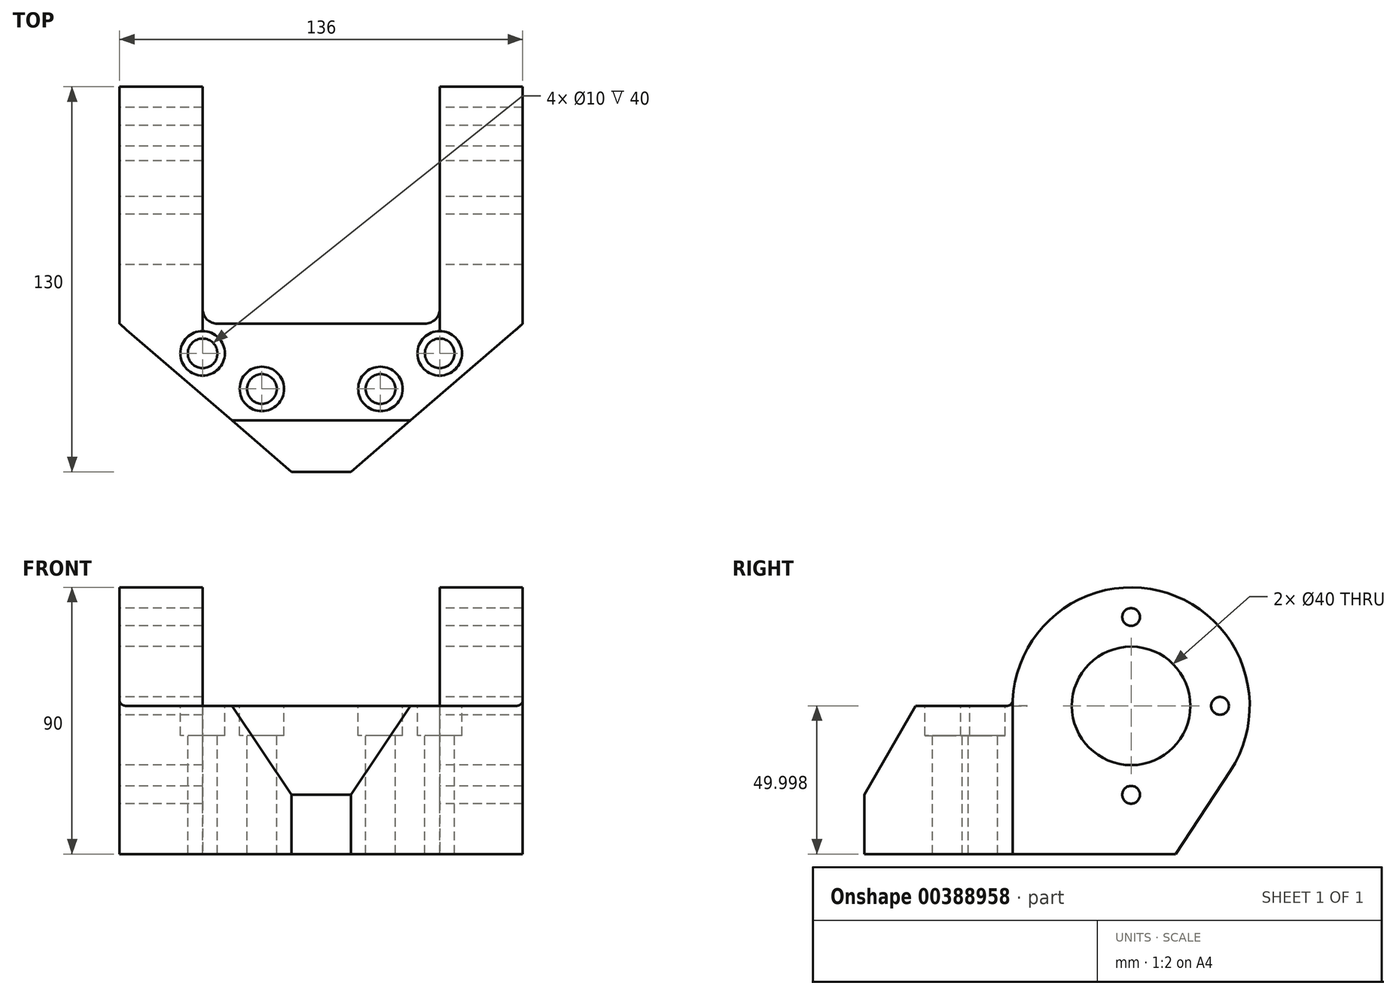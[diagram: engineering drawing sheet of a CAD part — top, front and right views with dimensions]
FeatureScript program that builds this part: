
annotation { "Feature Type Name" : "Feature", "Feature Type Description" : "" }
export const myFeature = defineFeature(function(context is Context, id is Id, definition is map)
    precondition{}
    {
        {
            var Q0;
            Q0=qCreatedBy(makeId("Right.planeOp"),FACE);
            var sketch = newSketch(context, id + "F0", { "sketchPlane" : qUnion([Q0])});
            skLineSegment(sketch, "E0.bottom", {"start": v(52.5, -26.77) * mm, "end": v(-52.5, -26.77) * mm});
            skPoint(sketch, "E0.middle", {"position": v(0, 0) * mm});
            skPoint(sketch, "E1", {"position": v(-52.5, -6.77) * mm});
            skLineSegment(sketch, "E2", {"start": v(-52.5, -6.77) * mm, "end": v(-35.18, 23.23) * mm});
            skPoint(sketch, "E3", {"position": v(37.5, 23.23) * mm});
            skLineSegment(sketch, "E4", {"start": v(-52.5, -26.77) * mm, "end": v(-52.5, -6.77) * mm});
            skCircle(sketch, "E5", {"center": v(37.5, 23.23) * mm, "radius": 40 * mm, "construction": true});
            skLineSegment(sketch, "E6", {"start": v(-52.5, -6.77) * mm, "end": v(-52.5, 23.23) * mm, "construction": true});
            skLineSegment(sketch, "E7", {"start": v(-52.5, 23.23) * mm, "end": v(37.5, 23.23) * mm, "construction": true});
            skLineSegment(sketch, "E8", {"start": v(-35.18, 23.23) * mm, "end": v(-2.5, 23.23) * mm});
            skLineSegment(sketch, "E9", {"start": v(52.5, -26.77) * mm, "end": v(70.92, 1.26) * mm});
            skArc(sketch, "E10", {"start": v(-2.5, 23.23) * mm, "mid": v(48.97, 61.55) * mm, "end": v(70.92, 1.26) * mm});
            skCircle(sketch, "E11", {"center": v(37.5, 23.23) * mm, "radius": 20 * mm});
            skCircle(sketch, "E12", {"center": v(37.5, -6.77) * mm, "radius": 3 * mm});
            skCircle(sketch, "E13", {"center": v(37.5, 53.23) * mm, "radius": 3 * mm});
            skCircle(sketch, "E14", {"center": v(67.5, 23.23) * mm, "radius": 3 * mm});
            skLineSegment(sketch, "E15", {"start": v(37.5, 23.23) * mm, "end": v(37.5, -6.77) * mm, "construction": true});
            skLineSegment(sketch, "E16", {"start": v(37.5, 23.23) * mm, "end": v(67.5, 23.23) * mm, "construction": true});
            skLineSegment(sketch, "E17", {"start": v(52.5, -26.77) * mm, "end": v(77.5, -26.77) * mm});
            skLineSegment(sketch, "E18", {"start": v(77.5, -26.77) * mm, "end": v(77.5, 23.23) * mm});
            skSolve(sketch);
        }
        {
            var Q0;
            Q0=makeQuery(id+"F0.imprint","IMPRINT",FACE,{"disambiguationData":[TD([[makeQuery(id+"F0.imprint","IMPRINT",EDGE,{"derivedFrom":sQuery(id+"F0.wireOp",EDGE,"E0.bottom")}),-1.0]])]});
            extrude(context, id + "F1", {"entities" : qUnion([Q0]), "endBound" : BoundingType.SYMMETRIC, "depth" : 136 * mm});
        }
        {
            var Q0;
            Q0=makeQuery(id+"F1.opExtrude","SWEPT_FACE",FACE,{"disambiguationData":[OSD([sQuery(id+"F0.wireOp",EDGE,"E0.bottom"),sQuery(id+"F0.wireOp",EDGE,"E17")])]});
            var sketch = newSketch(context, id + "F2", { "sketchPlane" : qUnion([Q0])});
            skLineSegment(sketch, "E19.bottom", {"start": v(40, -77.5) * mm, "end": v(-40, -77.5) * mm});
            skLineSegment(sketch, "E19.top", {"start": v(40, 2.5) * mm, "end": v(-40, 2.5) * mm});
            skLineSegment(sketch, "E19.left", {"start": v(40, -77.5) * mm, "end": v(40, 2.5) * mm});
            skLineSegment(sketch, "E19.right", {"start": v(-40, -77.5) * mm, "end": v(-40, 2.5) * mm});
            skLineSegment(sketch, "E20", {"start": v(-68, 2.5) * mm, "end": v(-10, 52.5) * mm});
            skLineSegment(sketch, "E21", {"start": v(68, 2.5) * mm, "end": v(10, 52.5) * mm});
            skSolve(sketch);
        }
        {
            var Q0;
            {var subQ0=sQuery(id+"F2.wireOp",EDGE,"E19.bottom");Q0=makeQuery(id+"F2.imprint","IMPRINT",FACE,{"disambiguationData":[TD([[makeQuery(id+"F2.imprint","IMPRINT",EDGE,{"derivedFrom":subQ0}),-1.0]])]});}
            var Q1;
            {var subQ0=sQuery(id+"F2.wireOp",EDGE,"E19.top");Q1=makeQuery(id+"F2.imprint","IMPRINT",FACE,{"disambiguationData":[TD([[makeQuery(id+"F2.imprint","IMPRINT",EDGE,{"derivedFrom":subQ0}),1.0]])]});}
            var Q2;
            {var subQ0=sQuery(id+"F2.wireOp",EDGE,"E21");Q2=makeQuery(id+"F2.imprint","IMPRINT",FACE,{"disambiguationData":[TD([[makeQuery(id+"F2.imprint","IMPRINT",EDGE,{"derivedFrom":subQ0}),-1.0]])]});}
            var Q3;
            {var subQ0=sQuery(id+"F2.wireOp",EDGE,"E20");Q3=makeQuery(id+"F2.imprint","IMPRINT",FACE,{"disambiguationData":[TD([[makeQuery(id+"F2.imprint","IMPRINT",EDGE,{"derivedFrom":subQ0}),1.0]])]});}
            extrude(context, id + "F3", {"entities" : qUnion([Q0, Q1, Q2, Q3]), "operationType" : NewBodyOperationType.REMOVE, "oppositeDirection" : true, "depth" : 90 * mm});
        }
        {
            var Q0;
            {var subQ0=sQuery(id+"F0.wireOp",EDGE,"E8");var subQ1=makeQuery(id+"F1.opExtrude","SWEPT_FACE",FACE,{"disambiguationData":[OSD([subQ0])]});var subQ2=sQuery(id+"F0.wireOp",EDGE,"E10");var subQ3=makeQuery(id+"F1.opExtrude","SWEPT_FACE",FACE,{"disambiguationData":[OSD([subQ2])]});Q0=makeQuery(id+"F3.boolean.opBoolean","SPLIT",EDGE,{"disambiguationData":[topologyDisambiguationEdgeConnected([subQ1,subQ3]),TD([makeQuery(id+"F3.opExtrude","SWEPT_FACE",FACE,{"disambiguationData":[OSD([sQuery(id+"F2.wireOp",EDGE,"E19.left")])]})])],"derivedFrom":makeQuery(id+"F1.opExtrude","SWEPT_EDGE",EDGE,{"disambiguationData":[OSD([subQ0,subQ2])]})});}
            var Q1;
            {var subQ0=sQuery(id+"F0.wireOp",EDGE,"E10");var subQ1=makeQuery(id+"F1.opExtrude","SWEPT_FACE",FACE,{"disambiguationData":[OSD([subQ0])]});var subQ2=sQuery(id+"F0.wireOp",EDGE,"E8");var subQ3=makeQuery(id+"F1.opExtrude","SWEPT_FACE",FACE,{"disambiguationData":[OSD([subQ2])]});Q1=makeQuery(id+"F3.boolean.opBoolean","SPLIT",EDGE,{"disambiguationData":[topologyDisambiguationEdgeConnected([subQ3,subQ1]),TD([makeQuery(id+"F3.opExtrude","SWEPT_FACE",FACE,{"disambiguationData":[OSD([sQuery(id+"F2.wireOp",EDGE,"E19.right")])]})])],"derivedFrom":makeQuery(id+"F1.opExtrude","SWEPT_EDGE",EDGE,{"disambiguationData":[OSD([subQ2,subQ0])]})});}
            fillet(context, id + "F4", {"entities" : qUnion([Q0, Q1]), "radius" : 2 * mm, "tangentPropagation" : true, "allowEdgeOverflow" : false});
        }
        {
            var Q0;
            Q0=makeQuery(id+"F3.boolean.opBoolean","COPY",EDGE,{"derivedFrom":makeQuery(id+"F3.opExtrude","SWEPT_EDGE",EDGE,{"disambiguationData":[OSD([sQuery(id+"F2.wireOp",EDGE,"E19.top"),sQuery(id+"F2.wireOp",EDGE,"E19.left")])]})});
            var Q1;
            Q1=makeQuery(id+"F3.boolean.opBoolean","COPY",EDGE,{"derivedFrom":makeQuery(id+"F3.opExtrude","SWEPT_EDGE",EDGE,{"disambiguationData":[OSD([sQuery(id+"F2.wireOp",EDGE,"E19.top"),sQuery(id+"F2.wireOp",EDGE,"E19.right")])]})});
            fillet(context, id + "F5", {"entities" : qUnion([Q0, Q1]), "radius" : 5 * mm, "tangentPropagation" : true, "allowEdgeOverflow" : false});
        }
        {
            var Q0;
            Q0=makeQuery(id+"F1.opExtrude","SWEPT_FACE",FACE,{"disambiguationData":[OSD([sQuery(id+"F0.wireOp",EDGE,"E8")])]});
            var sketch = newSketch(context, id + "F6", { "sketchPlane" : qUnion([Q0])});
            skCircle(sketch, "E22", {"center": v(40, -12.5) * mm, "radius": 5 * mm});
            skCircle(sketch, "E23", {"center": v(40, -12.5) * mm, "radius": 7.5 * mm});
            skCircle(sketch, "E24", {"center": v(20, -24.5) * mm, "radius": 5 * mm});
            skCircle(sketch, "E25", {"center": v(20, -24.5) * mm, "radius": 7.5 * mm});
            skCircle(sketch, "E26", {"center": v(-20, -24.5) * mm, "radius": 5 * mm});
            skCircle(sketch, "E27", {"center": v(-20, -24.5) * mm, "radius": 7.5 * mm});
            skCircle(sketch, "E28", {"center": v(-40, -12.5) * mm, "radius": 5 * mm});
            skCircle(sketch, "E29", {"center": v(-40, -12.5) * mm, "radius": 7.5 * mm});
            skSolve(sketch);
        }
        {
            var Q0;
            Q0 = qSketchRegion(id + "F6", true);
            extrude(context, id + "F7", {"entities" : qUnion([Q0]), "operationType" : NewBodyOperationType.REMOVE, "oppositeDirection" : true, "depth" : 10 * mm});
        }
        {
            var Q0;
            Q0=makeQuery(id+"F7.boolean.opBoolean","SPLIT",FACE,{"disambiguationData":[TD([makeQuery(id+"F7.opExtrude","SWEPT_FACE",FACE,{"disambiguationData":[OSD([sQuery(id+"F6.wireOp",EDGE,"E28")])]})])],"derivedFrom":makeQuery(id+"F1.opExtrude","SWEPT_FACE",FACE,{"disambiguationData":[OSD([sQuery(id+"F0.wireOp",EDGE,"E8")])]})});
            var Q1;
            Q1=makeQuery(id+"F7.boolean.opBoolean","SPLIT",FACE,{"disambiguationData":[TD([makeQuery(id+"F7.opExtrude","SWEPT_FACE",FACE,{"disambiguationData":[OSD([sQuery(id+"F6.wireOp",EDGE,"E26")])]})])],"derivedFrom":makeQuery(id+"F1.opExtrude","SWEPT_FACE",FACE,{"disambiguationData":[OSD([sQuery(id+"F0.wireOp",EDGE,"E8")])]})});
            var Q2;
            Q2=makeQuery(id+"F7.boolean.opBoolean","SPLIT",FACE,{"disambiguationData":[TD([makeQuery(id+"F7.opExtrude","SWEPT_FACE",FACE,{"disambiguationData":[OSD([sQuery(id+"F6.wireOp",EDGE,"E24")])]})])],"derivedFrom":makeQuery(id+"F1.opExtrude","SWEPT_FACE",FACE,{"disambiguationData":[OSD([sQuery(id+"F0.wireOp",EDGE,"E8")])]})});
            var Q3;
            Q3=makeQuery(id+"F7.boolean.opBoolean","SPLIT",FACE,{"disambiguationData":[TD([makeQuery(id+"F7.opExtrude","SWEPT_FACE",FACE,{"disambiguationData":[OSD([sQuery(id+"F6.wireOp",EDGE,"E22")])]})])],"derivedFrom":makeQuery(id+"F1.opExtrude","SWEPT_FACE",FACE,{"disambiguationData":[OSD([sQuery(id+"F0.wireOp",EDGE,"E8")])]})});
            extrude(context, id + "F8", {"entities" : qUnion([Q0, Q1, Q2, Q3]), "operationType" : NewBodyOperationType.REMOVE, "oppositeDirection" : true, "depth" : 50 * mm});
        }
    });
